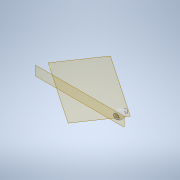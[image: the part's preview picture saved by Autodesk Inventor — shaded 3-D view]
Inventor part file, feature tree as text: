
AUTODESK INVENTOR PART (.ipt)
format: ipt  version: 2020 (Build 240168000, 168)  size: 188,416 bytes
history: native  units: mm
features: sketch x5, plane x4, extrude x3, other x3, revolve x1, reference x1, projected_geometry x1
ambient origin geometry x8: Origin, YZ Plane, XZ Plane, XY Plane, X Axis, Y Axis, Z Axis, Center Point
bodies: Volumenkörper1 (feature_tree)
feature tree (18):
  extrude  "Extrusion1"  Depth=3.0mm TaperAngle=0.0deg
  sketch  "Skizze2"  dims[d6=3.0mm d8=8.5mm]
  plane  "Arbeitsebene2"
  revolve  "Umdrehung2"
  extrude  "Extrusion3"  Depth=8.5mm
  sketch  "Skizze7"  dims[d12=5.0mm]
  plane  "Arbeitsebene4"
  extrude  "Extrusion4"  Depth=7.247mm TaperAngle=0.0deg
  sketch  "Skizze1"  dims[d0=4.0mm d1=3.0mm d2=0.0mm]
  reference  "Referenz1"
  plane  "Arbeitsebene1"
  sketch  "Skizze5"  dims[d9=90.0deg d10=7.247mm d11=0.0mm]
  projected_geometry  "Projizierte Kontur1"
  plane  "Arbeitsebene3"
  sketch  "Skizze8"  dims[d13=8.0mm d14=0.0mm]
  parser-record x1  (decoder bookkeeping rows leaked as tree rows — omitted from the tree; the rows remain in map.json)
  other  "GlassesAssembly.iam"
  other  "CameraArm:1"
note: 1 file-system path scrubbed to <path> (originals preserved in map.json)
